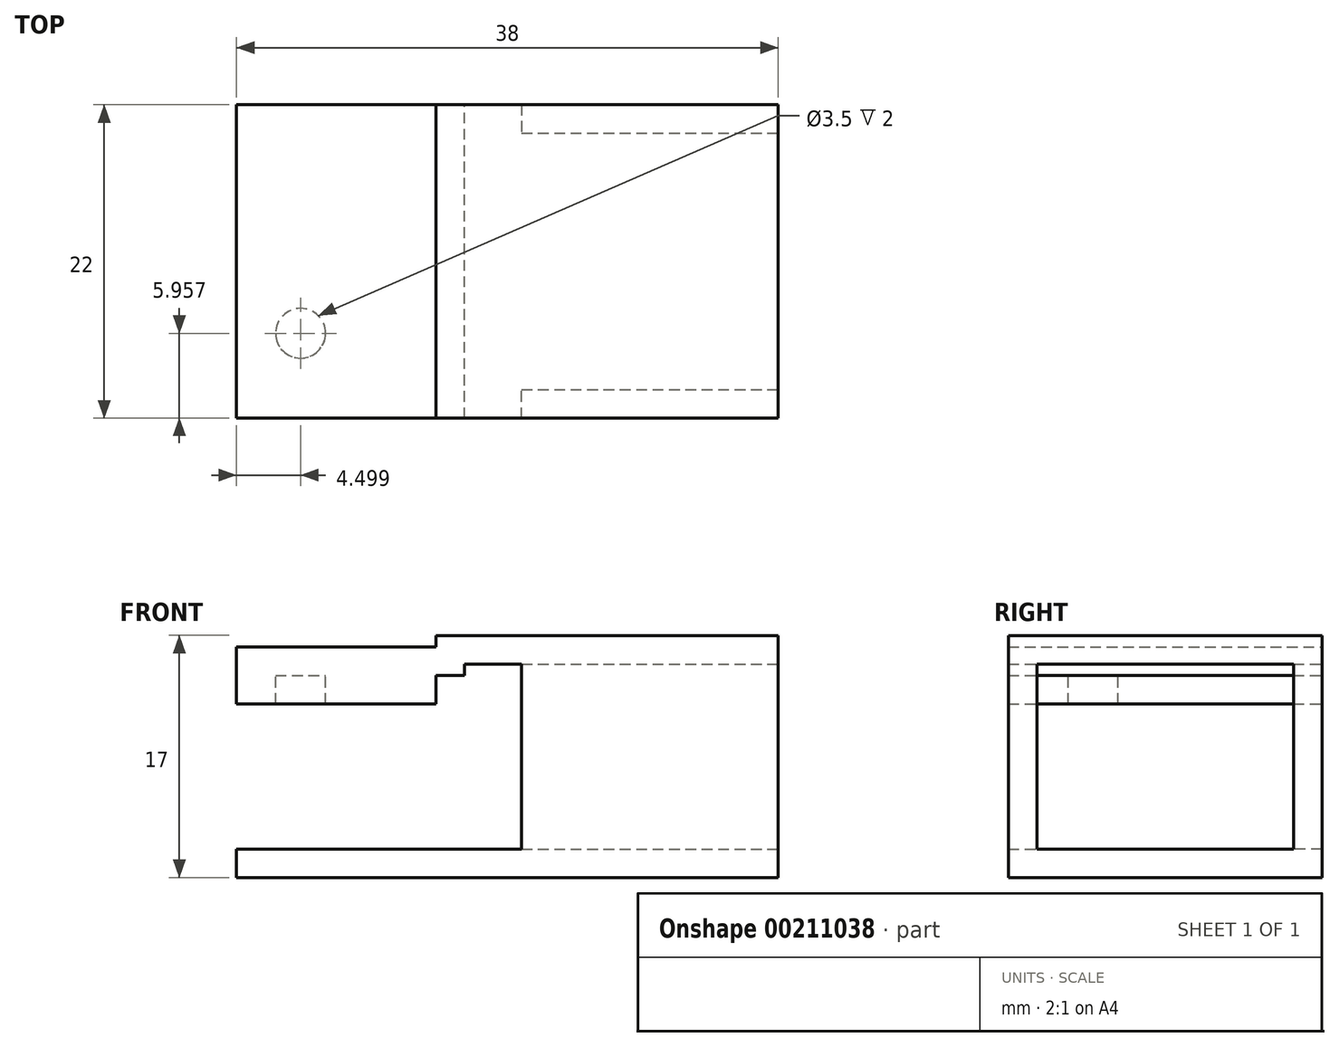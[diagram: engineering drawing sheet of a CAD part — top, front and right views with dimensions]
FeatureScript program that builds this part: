
annotation { "Feature Type Name" : "Feature", "Feature Type Description" : "" }
export const myFeature = defineFeature(function(context is Context, id is Id, definition is map)
    precondition{}
    {
        {
            var Q0;
            Q0=qCreatedBy(makeId("Front.planeOp"),FACE);
            var sketch = newSketch(context, id + "F0", { "sketchPlane" : qUnion([Q0])});
            skLineSegment(sketch, "E0.bottom", {"start": v(-39.94, 30.46) * mm, "end": v(-3.94, 30.46) * mm});
            skLineSegment(sketch, "E0.top", {"start": v(-39.94, 17.46) * mm, "end": v(-3.94, 17.46) * mm});
            skLineSegment(sketch, "E0.left", {"start": v(-39.94, 30.46) * mm, "end": v(-39.94, 17.46) * mm});
            skLineSegment(sketch, "E0.right", {"start": v(-3.94, 30.46) * mm, "end": v(-3.94, 17.46) * mm});
            skLineSegment(sketch, "E1", {"start": v(-23.94, 30.46) * mm, "end": v(-23.94, 17.46) * mm});
            skLineSegment(sketch, "E2", {"start": v(-23.94, 29.66) * mm, "end": v(-39.94, 29.66) * mm});
            skSolve(sketch);
        }
        {
            var Q0;
            {var subQ5=sQuery(id+"F0.wireOp",EDGE,"E2");Q0=makeQuery(id+"F0.imprint","IMPRINT",FACE,{"disambiguationData":[TD([[makeQuery(id+"F0.imprint","IMPRINT",EDGE,{"derivedFrom":subQ5}),1.0]])]});}
            var Q1;
            {var subQ4=sQuery(id+"F0.wireOp",EDGE,"E0.right");Q1=makeQuery(id+"F0.imprint","IMPRINT",FACE,{"disambiguationData":[TD([[makeQuery(id+"F0.imprint","IMPRINT",EDGE,{"derivedFrom":subQ4}),-1.0]])]});}
            extrude(context, id + "F1", {"entities" : qUnion([Q0, Q1]), "depth" : 18 * mm});
        }
        {
            var Q0;
            Q0=makeQuery(id+"F1.opExtrude","SWEPT_FACE",FACE,{"disambiguationData":[OSD([sQuery(id+"F0.wireOp",EDGE,"E0.left")])]});
            var Q1;
            Q1=makeQuery(id+"F1.opExtrude","CAP_FACE",FACE,{"disambiguationData":[OSD([sQuery(id+"F0.wireOp",EDGE,"E0.bottom"),sQuery(id+"F0.wireOp",EDGE,"E0.top"),sQuery(id+"F0.wireOp",EDGE,"E0.left"),sQuery(id+"F0.wireOp",EDGE,"E0.right"),sQuery(id+"F0.wireOp",EDGE,"E1"),sQuery(id+"F0.wireOp",EDGE,"E2")])],"isStart":false});
            var Q2;
            Q2=makeQuery(id+"F1.opExtrude","CAP_FACE",FACE,{"disambiguationData":[OSD([sQuery(id+"F0.wireOp",EDGE,"E0.bottom"),sQuery(id+"F0.wireOp",EDGE,"E0.top"),sQuery(id+"F0.wireOp",EDGE,"E0.left"),sQuery(id+"F0.wireOp",EDGE,"E0.right"),sQuery(id+"F0.wireOp",EDGE,"E1"),sQuery(id+"F0.wireOp",EDGE,"E2")])],"isStart":true});
            shell(context, id + "F2", {"entities" : qUnion([Q0, Q1, Q2]), "thickness" : 2 * mm, "oppositeDirection" : true});
        }
        {
            var Q0;
            Q0=makeQuery(id+"F1.opExtrude","CAP_FACE",FACE,{"disambiguationData":[OSD([sQuery(id+"F0.wireOp",EDGE,"E0.bottom"),sQuery(id+"F0.wireOp",EDGE,"E0.top"),sQuery(id+"F0.wireOp",EDGE,"E0.left"),sQuery(id+"F0.wireOp",EDGE,"E0.right"),sQuery(id+"F0.wireOp",EDGE,"E1"),sQuery(id+"F0.wireOp",EDGE,"E2")])],"isStart":false});
            var sketch = newSketch(context, id + "F3", { "sketchPlane" : qUnion([Q0])});
            skLineSegment(sketch, "E3", {"start": v(-19.94, 32.46) * mm, "end": v(-19.94, 15.46) * mm});
            skSolve(sketch);
        }
        {
            var Q0;
            Q0 = qSketchRegion(id + "F3", true);
            var Q1;
            {var subQ0=sQuery(id+"F0.wireOp",EDGE,"E0.right");var subQ1=makeQuery(id+"F1.opExtrude","CAP_EDGE",EDGE,{"disambiguationData":[OSD([subQ0])],"isStart":false});Q1=makeQuery(id+"F3.imprint","IMPRINT",FACE,{"disambiguationData":[TD([[makeQuery(id+"F3.imprint","IMPRINT",EDGE,{"derivedFrom":subQ1}),-1.0]])]});}
            var Q2;
            {var subQ7=sQuery(id+"F0.wireOp",EDGE,"E0.right");var subQ8=makeQuery(id+"F2.opShell","OFFSET_EDGE",EDGE,{"disambiguationData":[OSD([subQ7]),TDD([makeQuery(id+"F1.opExtrude","CAP_EDGE",EDGE,{"disambiguationData":[OSD([subQ7])],"isStart":false})])]});Q2=makeQuery(id+"F3.imprint","IMPRINT",FACE,{"disambiguationData":[TD([[makeQuery(id+"F3.imprint","IMPRINT",EDGE,{"derivedFrom":subQ8}),-1.0]])]});}
            var Q3;
            {var subQ2=sQuery(id+"F0.wireOp",EDGE,"E1");var subQ3=makeQuery(id+"F1.opExtrude","CAP_EDGE",EDGE,{"disambiguationData":[OSD([subQ2])],"isStart":false});Q3=makeQuery(id+"F3.imprint","IMPRINT",FACE,{"disambiguationData":[TD([[makeQuery(id+"F3.imprint","IMPRINT",EDGE,{"derivedFrom":subQ3}),1.0]])]});}
            var Q4;
            {var subQ6=sQuery(id+"F0.wireOp",EDGE,"E0.left");var subQ7=makeQuery(id+"F2.opShell","OFFSET_EDGE",EDGE,{"disambiguationData":[OSD([subQ6]),TDD([makeQuery(id+"F1.opExtrude","CAP_EDGE",EDGE,{"disambiguationData":[OSD([subQ6])],"isStart":false})])]});Q4=makeQuery(id+"F3.imprint","IMPRINT",FACE,{"disambiguationData":[TD([[makeQuery(id+"F3.imprint","IMPRINT",EDGE,{"derivedFrom":subQ7}),1.0]])]});}
            extrude(context, id + "F4", {"entities" : qUnion([Q0, Q1, Q2, Q3, Q4]), "operationType" : NewBodyOperationType.ADD, "depth" : 2 * mm});
        }
        {
            var Q0;
            Q0=makeQuery(id+"F1.opExtrude","CAP_FACE",FACE,{"disambiguationData":[OSD([sQuery(id+"F0.wireOp",EDGE,"E0.bottom"),sQuery(id+"F0.wireOp",EDGE,"E0.top"),sQuery(id+"F0.wireOp",EDGE,"E0.left"),sQuery(id+"F0.wireOp",EDGE,"E0.right"),sQuery(id+"F0.wireOp",EDGE,"E1"),sQuery(id+"F0.wireOp",EDGE,"E2")])],"isStart":true});
            var sketch = newSketch(context, id + "F5", { "sketchPlane" : qUnion([Q0])});
            skLineSegment(sketch, "E4.0", {"start": v(19.94, 30.46) * mm, "end": v(19.94, 17.46) * mm});
            skLineSegment(sketch, "E5", {"start": v(19.94, 30.46) * mm, "end": v(19.94, 32.46) * mm});
            skLineSegment(sketch, "E6", {"start": v(19.94, 17.46) * mm, "end": v(19.94, 15.46) * mm});
            skSolve(sketch);
        }
        {
            var Q0;
            {var subQ9=sQuery(id+"F5.wireOp",EDGE,"E5");Q0=makeQuery(id+"F5.imprint","IMPRINT",FACE,{"disambiguationData":[TD([[makeQuery(id+"F5.imprint","IMPRINT",EDGE,{"derivedFrom":subQ9}),1.0]])]});}
            var Q1;
            {var subQ0=sQuery(id+"F5.wireOp",EDGE,"E4.0");Q1=makeQuery(id+"F5.imprint","IMPRINT",FACE,{"disambiguationData":[TD([[makeQuery(id+"F5.imprint","IMPRINT",EDGE,{"derivedFrom":subQ0}),-1.0]])]});}
            var Q2;
            {var subQ0=sQuery(id+"F5.wireOp",EDGE,"E6");Q2=makeQuery(id+"F5.imprint","IMPRINT",FACE,{"disambiguationData":[TD([[makeQuery(id+"F5.imprint","IMPRINT",EDGE,{"derivedFrom":subQ0}),1.0]])]});}
            var Q3;
            {var subQ3=sQuery(id+"F5.wireOp",EDGE,"E5");Q3=makeQuery(id+"F5.imprint","IMPRINT",FACE,{"disambiguationData":[TD([[makeQuery(id+"F5.imprint","IMPRINT",EDGE,{"derivedFrom":subQ3}),-1.0]])]});}
            extrude(context, id + "F6", {"entities" : qUnion([Q0, Q1, Q2, Q3]), "operationType" : NewBodyOperationType.ADD, "depth" : 2 * mm});
        }
        {
            var Q0;
            {var subQ0=sQuery(id+"F0.wireOp",EDGE,"E2");Q0=makeQuery(id+"F4.boolean.opBoolean","MERGE",FACE,{"derivedFrom":[makeQuery(id+"F1.opExtrude","SWEPT_FACE",FACE,{"disambiguationData":[OSD([subQ0])]}),makeQuery(id+"F4.opExtrude","SWEPT_FACE",FACE,{"disambiguationData":[OSD([subQ0]),TDD([makeQuery(id+"F3.imprint","IMPRINT",EDGE,{"derivedFrom":makeQuery(id+"F1.opExtrude","CAP_EDGE",EDGE,{"disambiguationData":[OSD([subQ0])],"isStart":false})})])]})]});}
            var sketch = newSketch(context, id + "F7", { "sketchPlane" : qUnion([Q0])});
            skCircle(sketch, "E7", {"center": v(-35.44, -3.96) * mm, "radius": 1.75 * mm});
            skLineSegment(sketch, "E8", {"start": v(-25.94, -9) * mm, "end": v(-30.17, -9) * mm});
            skCircle(sketch, "E9.MirrorC", {"center": v(-35.44, -14.04) * mm, "radius": 1.75 * mm});
            skSolve(sketch);
        }
        {
            var Q0;
            Q0=makeQuery(id+"F7.imprint","IMPRINT",FACE,{"disambiguationData":[TD([[makeQuery(id+"F7.imprint","IMPRINT",EDGE,{"derivedFrom":sQuery(id+"F7.wireOp",EDGE,"E7")}),1.0]])]});
            var Q1;
            Q1=makeQuery(id+"F7.imprint","IMPRINT",FACE,{"disambiguationData":[TD([[makeQuery(id+"F7.imprint","IMPRINT",EDGE,{"derivedFrom":sQuery(id+"F7.wireOp",EDGE,"E9.MirrorC")}),-1.0]])]});
            extrude(context, id + "F8", {"entities" : qUnion([Q0, Q1]), "operationType" : NewBodyOperationType.ADD, "oppositeDirection" : true, "depth" : 4 * mm});
        }
        {
            var Q0;
            Q0=makeQuery(id+"F2.opShell","OFFSET_FACE",FACE,{"disambiguationData":[OSD([sQuery(id+"F0.wireOp",EDGE,"E0.right")])]});
            extrude(context, id + "F9", {"entities" : qUnion([Q0]), "operationType" : NewBodyOperationType.REMOVE, "oppositeDirection" : true, "depth" : 25 * mm});
        }
    });
